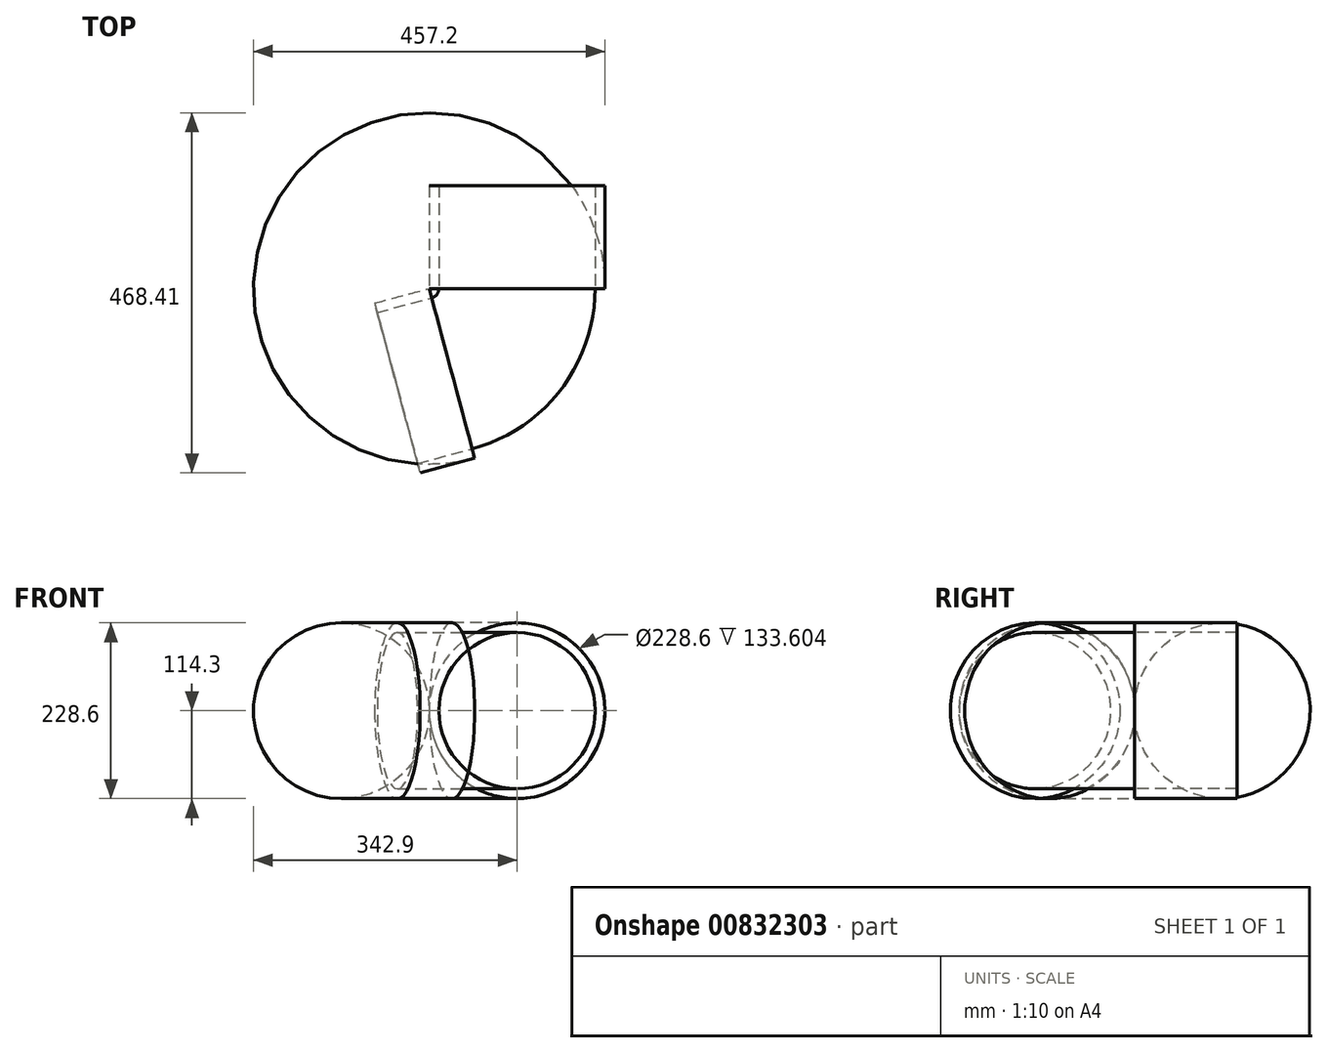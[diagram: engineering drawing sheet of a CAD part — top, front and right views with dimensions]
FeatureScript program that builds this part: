
annotation { "Feature Type Name" : "Feature", "Feature Type Description" : "" }
export const myFeature = defineFeature(function(context is Context, id is Id, definition is map)
    precondition{}
    {
        {
            var Q0;
            Q0=qCreatedBy(makeId("Front.planeOp"),FACE);
            var sketch = newSketch(context, id + "F0", { "sketchPlane" : qUnion([Q0])});
            skCircle(sketch, "E0", {"center": v(0, 0) * mm, "radius": 114.3 * mm});
            skCircle(sketch, "E1", {"center": v(0, 0) * mm, "radius": 101.6 * mm});
            skLineSegment(sketch, "E2", {"start": v(-114.3, 202.5) * mm, "end": v(-114.3, -26.1) * mm, "construction": true});
            skSolve(sketch);
        }
        {
            var Q0;
            Q0 = qSketchRegion(id + "F0", true);
            extrude(context, id + "F1", {"entities" : qUnion([Q0]), "oppositeDirection" : true, "depth" : 133.6 * mm, "offsetDistance" : 25.4 * mm});
        }
        {
            var Q0;
            Q0=makeQuery(id+"F1.opExtrude","CAP_FACE",FACE,{"disambiguationData":[OSD([sQuery(id+"F0.wireOp",EDGE,"E0"),sQuery(id+"F0.wireOp",EDGE,"E1")])],"isStart":true});
            var Q1;
            Q1=sQuery(id+"F0.wireOp",EDGE,"E2");
            revolve(context, id + "F2", {"operationType" : NewBodyOperationType.ADD, "surfaceOperationType" : NewSurfaceOperationType.NEW, "entities" : qUnion([Q0]), "axis" : qUnion([Q1]), "revolveType" : RevolveType.ONE_DIRECTION, "angle" : 75 * degree});
        }
        {
            var Q0;
            Q0=makeQuery(id+"F2.opRevolve","CAP_FACE",FACE,{"disambiguationData":[OSD([sQuery(id+"F0.wireOp",EDGE,"E0"),sQuery(id+"F0.wireOp",EDGE,"E1")])],"isStart":false});
            extrude(context, id + "F3", {"entities" : qUnion([Q0]), "operationType" : NewBodyOperationType.ADD, "depth" : 73.4 * mm, "offsetDistance" : 25.4 * mm});
        }
    });
